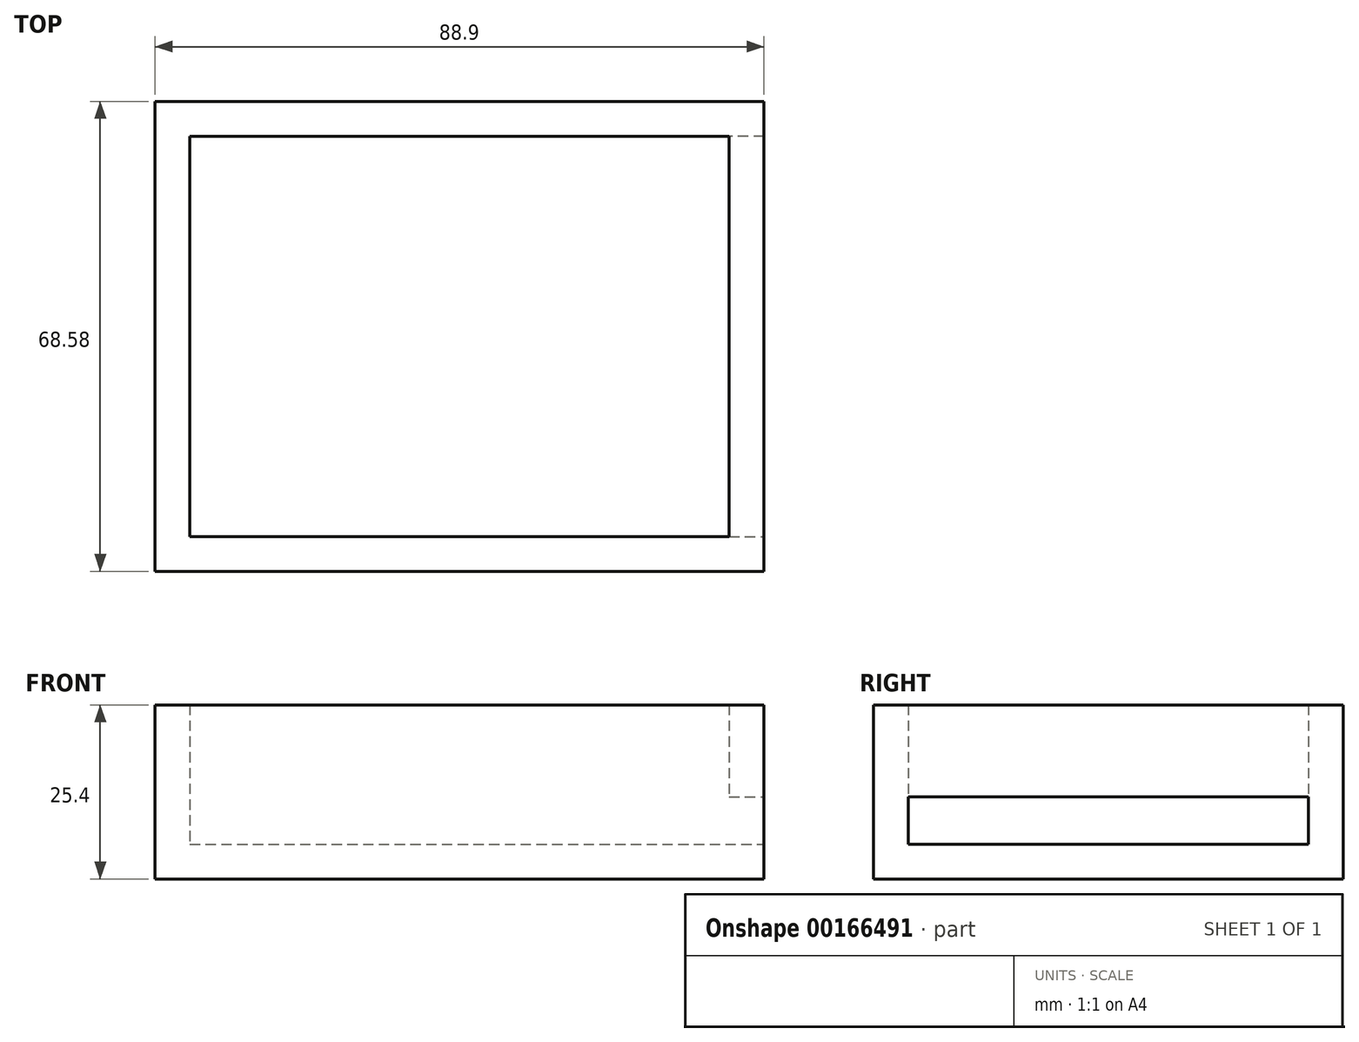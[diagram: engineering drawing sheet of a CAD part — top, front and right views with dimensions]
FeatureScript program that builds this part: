
annotation { "Feature Type Name" : "Feature", "Feature Type Description" : "" }
export const myFeature = defineFeature(function(context is Context, id is Id, definition is map)
    precondition{}
    {
        {
            var Q0;
            Q0=qCreatedBy(makeId("Top.planeOp"),FACE);
            var sketch = newSketch(context, id + "F0", { "sketchPlane" : qUnion([Q0])});
            skLineSegment(sketch, "E0", {"start": v(0, 0) * mm, "end": v(88.9, 0) * mm});
            skLineSegment(sketch, "E1", {"start": v(88.9, 0) * mm, "end": v(88.9, 68.58) * mm});
            skLineSegment(sketch, "E2", {"start": v(88.9, 68.58) * mm, "end": v(0, 68.58) * mm});
            skLineSegment(sketch, "E3", {"start": v(0, 68.58) * mm, "end": v(0, 0) * mm});
            skPoint(sketch, "E4", {"position": v(5.08, 5.08) * mm});
            skPoint(sketch, "E5", {"position": v(83.82, 5.08) * mm});
            skPoint(sketch, "E6", {"position": v(83.82, 63.5) * mm});
            skPoint(sketch, "E7", {"position": v(5.08, 63.5) * mm});
            skLineSegment(sketch, "E8", {"start": v(5.08, 5.08) * mm, "end": v(83.82, 5.08) * mm});
            skLineSegment(sketch, "E9", {"start": v(83.82, 63.5) * mm, "end": v(83.82, 5.08) * mm});
            skLineSegment(sketch, "E10", {"start": v(83.82, 63.5) * mm, "end": v(5.08, 63.5) * mm});
            skLineSegment(sketch, "E11", {"start": v(5.08, 5.08) * mm, "end": v(5.08, 63.5) * mm});
            skSolve(sketch);
        }
        {
            var Q0;
            Q0=makeQuery(id+"F0.imprint","IMPRINT",FACE,{"disambiguationData":[TD([[makeQuery(id+"F0.imprint","IMPRINT",EDGE,{"derivedFrom":sQuery(id+"F0.wireOp",EDGE,"E8")}),1.0]])]});
            extrude(context, id + "F1", {"entities" : qUnion([Q0]), "depth" : 5.08 * mm});
        }
        {
            var Q0;
            Q0=makeQuery(id+"F0.imprint","IMPRINT",FACE,{"disambiguationData":[TD([[makeQuery(id+"F0.imprint","IMPRINT",EDGE,{"derivedFrom":sQuery(id+"F0.wireOp",EDGE,"E0")}),1.0]])]});
            extrude(context, id + "F2", {"entities" : qUnion([Q0]), "operationType" : NewBodyOperationType.ADD, "depth" : 25.4 * mm});
        }
        {
            var Q0;
            Q0=makeQuery(id+"F2.opExtrude","SWEPT_FACE",FACE,{"disambiguationData":[OSD([sQuery(id+"F0.wireOp",EDGE,"E1")])]});
            var sketch = newSketch(context, id + "F3", { "sketchPlane" : qUnion([Q0])});
            skLineSegment(sketch, "E12.bottom", {"start": v(5.08, 11.96) * mm, "end": v(63.5, 11.96) * mm});
            skLineSegment(sketch, "E12.top", {"start": v(5.08, 5.08) * mm, "end": v(63.5, 5.08) * mm});
            skLineSegment(sketch, "E12.left", {"start": v(5.08, 11.96) * mm, "end": v(5.08, 5.08) * mm});
            skLineSegment(sketch, "E12.right", {"start": v(63.5, 11.96) * mm, "end": v(63.5, 5.08) * mm});
            skSolve(sketch);
        }
        {
            var Q0;
            Q0=makeQuery(id+"F3.imprint","IMPRINT",FACE,{"disambiguationData":[TD([[makeQuery(id+"F3.imprint","IMPRINT",EDGE,{"derivedFrom":sQuery(id+"F3.wireOp",EDGE,"E12.bottom")}),-1.0]])]});
            extrude(context, id + "F4", {"entities" : qUnion([Q0]), "operationType" : NewBodyOperationType.REMOVE, "oppositeDirection" : true, "depth" : 5.08 * mm});
        }
    });
